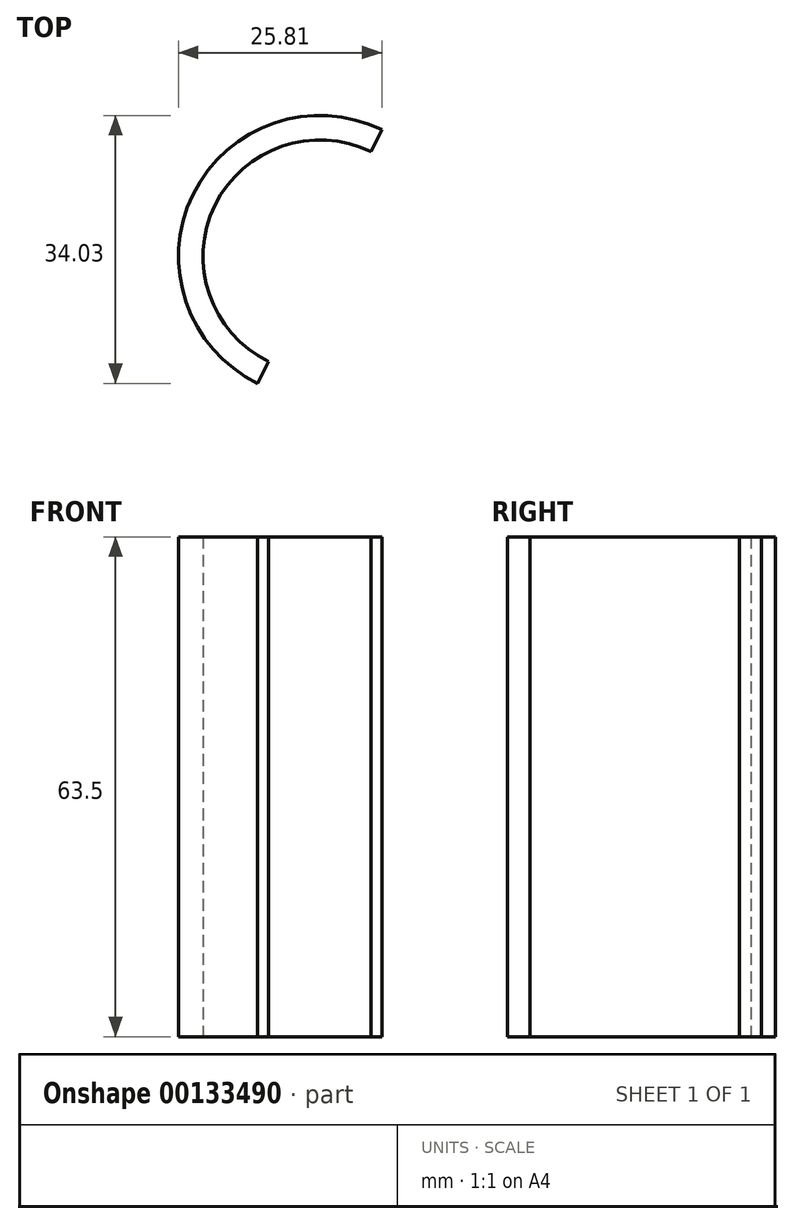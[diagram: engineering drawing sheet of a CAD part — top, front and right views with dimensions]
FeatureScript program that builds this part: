
annotation { "Feature Type Name" : "Feature", "Feature Type Description" : "" }
export const myFeature = defineFeature(function(context is Context, id is Id, definition is map)
    precondition{}
    {
        {
            var Q0;
            Q0=qCreatedBy(makeId("Top.planeOp"),FACE);
            var sketch = newSketch(context, id + "F0", { "sketchPlane" : qUnion([Q0])});
            skCircle(sketch, "E0", {"center": v(0, 0) * mm, "radius": 17.93 * mm});
            skCircle(sketch, "E1", {"center": v(0, 0) * mm, "radius": 14.81 * mm});
            skLineSegment(sketch, "E2", {"start": v(0, 0) * mm, "end": v(7.88, 16.1) * mm});
            skLineSegment(sketch, "E3", {"start": v(7.88, 16.1) * mm, "end": v(-7.88, -16.1) * mm});
            skSolve(sketch);
        }
        {
            var Q0;
            {var subQ0=sQuery(id+"F0.wireOp",EDGE,"E3");var subQ1=sQuery(id+"F0.wireOp",EDGE,"E0");var subQ2=makeQuery(id+"F0.imprint","INTERSECT",VERTEX,{"disambiguationData":[OD(0.0)],"derivedFrom":[subQ1,subQ0]});Q0=makeQuery(id+"F0.imprint","IMPRINT",FACE,{"disambiguationData":[TD([[makeQuery(id+"F0.imprint","IMPRINT",EDGE,{"disambiguationData":[TD([[subQ2,1.0]])],"derivedFrom":subQ1}),1.0]])]});}
            extrude(context, id + "F1", {"entities" : qUnion([Q0]), "depth" : 63.5 * mm});
        }
    });
